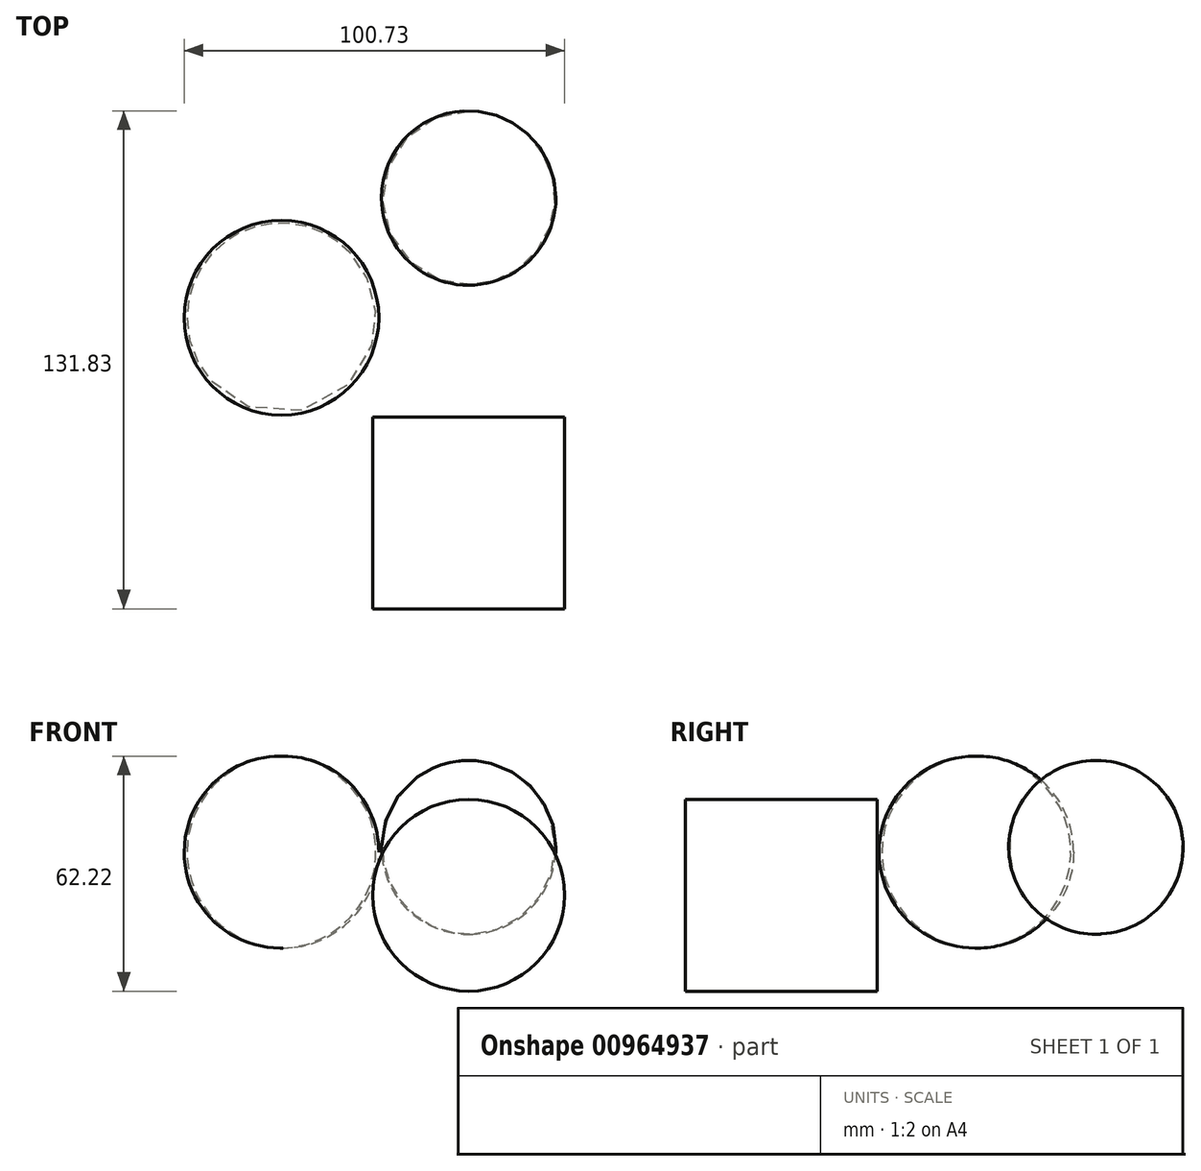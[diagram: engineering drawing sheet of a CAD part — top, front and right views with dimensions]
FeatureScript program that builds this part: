
annotation { "Feature Type Name" : "Feature", "Feature Type Description" : "" }
export const myFeature = defineFeature(function(context is Context, id is Id, definition is map)
    precondition{}
    {
        {
            var Q0;
            Q0=qCreatedBy(makeId("Front.planeOp"),FACE);
            var sketch = newSketch(context, id + "F0", { "sketchPlane" : qUnion([Q0])});
            skCircle(sketch, "E0", {"center": v(-49.2, 28.3) * mm, "radius": 25.4 * mm});
            skPoint(sketch, "E1", {"position": v(-49.56, 53.7) * mm});
            skPoint(sketch, "E2", {"position": v(-49.56, 2.9) * mm});
            skLineSegment(sketch, "E3", {"start": v(-49.56, 53.7) * mm, "end": v(-49.56, 2.9) * mm, "construction": true});
            skLineSegment(sketch, "E4", {"start": v(-49.56, 53.7) * mm, "end": v(-49.56, 2.9) * mm});
            skSolve(sketch);
        }
        {
            var Q0;
            Q0=qCreatedBy(makeId("Right.planeOp"),FACE);
            var sketch = newSketch(context, id + "F1", { "sketchPlane" : qUnion([Q0])});
            skLineSegment(sketch, "E5.bottom", {"start": v(-77.05, 16.87) * mm, "end": v(-26.25, 16.87) * mm});
            skLineSegment(sketch, "E5.top", {"start": v(-77.05, -8.53) * mm, "end": v(-26.25, -8.53) * mm});
            skLineSegment(sketch, "E5.left", {"start": v(-77.05, 16.87) * mm, "end": v(-77.05, -8.53) * mm});
            skLineSegment(sketch, "E5.right", {"start": v(-26.25, 16.87) * mm, "end": v(-26.25, -8.53) * mm});
            skLineSegment(sketch, "E6", {"start": v(-77.05, -2.18) * mm, "end": v(-26.25, -2.18) * mm, "construction": true});
            skSolve(sketch);
        }
        {
            var Q0;
            Q0=makeQuery(id+"F1.imprint","IMPRINT",FACE,{"disambiguationData":[TD([[makeQuery(id+"F1.imprint","IMPRINT",EDGE,{"derivedFrom":sQuery(id+"F1.wireOp",EDGE,"E5.bottom")}),-1.0]])]});
            var Q1;
            Q1=sQuery(id+"F1.wireOp",EDGE,"E5.bottom");
            var Q2;
            Q2=sQuery(id+"F1.wireOp",EDGE,"E5.bottom");
            revolve(context, id + "F2", {"surfaceOperationType" : NewSurfaceOperationType.NEW, "entities" : qUnion([Q0]), "surfaceEntities" : qUnion([Q1]), "axis" : qUnion([Q2]), "revolveType" : RevolveType.FULL});
        }
        {
            var Q0;
            {var subQ0=sQuery(id+"F0.wireOp",EDGE,"E4");Q0=makeQuery(id+"F0.imprint","IMPRINT",FACE,{"disambiguationData":[TD([[makeQuery(id+"F0.imprint","IMPRINT",EDGE,{"derivedFrom":subQ0}),1.0]])]});}
            var Q1;
            Q1=sQuery(id+"F0.wireOp",EDGE,"E4");
            revolve(context, id + "F3", {"surfaceOperationType" : NewSurfaceOperationType.NEW, "entities" : qUnion([Q0]), "axis" : qUnion([Q1]), "revolveType" : RevolveType.FULL});
        }
        {
            var Q0;
            Q0=qCreatedBy(makeId("Right.planeOp"),FACE);
            var sketch = newSketch(context, id + "F4", { "sketchPlane" : qUnion([Q0])});
            skArc(sketch, "E7", {"start": v(33.06, 6.6) * mm, "mid": v(54.74, 30.92) * mm, "end": v(30.32, 52.49) * mm});
            skLineSegment(sketch, "E8", {"start": v(30.32, 52.49) * mm, "end": v(33.06, 6.6) * mm, "construction": true});
            skLineSegment(sketch, "E9", {"start": v(30.32, 52.49) * mm, "end": v(33.06, 6.6) * mm});
            skSolve(sketch);
        }
        {
            var Q0;
            Q0 = qSketchRegion(id + "F4", true);
            var Q1;
            Q1=sQuery(id+"F4.wireOp",EDGE,"E8");
            revolve(context, id + "F5", {"surfaceOperationType" : NewSurfaceOperationType.NEW, "entities" : qUnion([Q0]), "axis" : qUnion([Q1]), "revolveType" : RevolveType.FULL});
        }
    });
